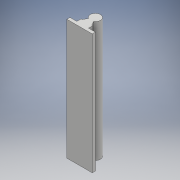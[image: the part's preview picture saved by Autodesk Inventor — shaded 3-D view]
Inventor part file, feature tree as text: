
AUTODESK INVENTOR PART (.ipt)
format: ipt  version: 2018 (Build 220112000, 112)  size: 112,640 bytes
history: native  units: mm
features: other x1, extrude x1, sketch x1
ambient origin geometry x8: Origin, YZ Plane, XZ Plane, XY Plane, X Axis, Y Axis, Z Axis, Center Point
bodies: Body1 (feature_tree)
feature tree (3):
  other  "Sólido1"
  extrude  "Extrusão1"  Depth=190.0mm
  sketch  "Esboço1"  dims[d6=16.0mm d7=25.0mm d8=18.5mm d9=11.7mm d10=8.0mm d11=30.0deg d12=30.0deg d13=5.0mm d14=40.0mm d15=190.0mm d16=0.0mm]
